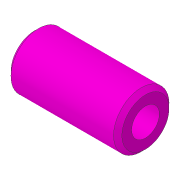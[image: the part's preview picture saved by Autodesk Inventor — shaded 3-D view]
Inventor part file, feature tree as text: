
AUTODESK INVENTOR PART (.ipt)
format: ipt  version: 2019.4 (Build 234330000, 330)  size: 90,112 bytes
history: native  units: mm
features: other x1, extrude x1, chamfer x1, sketch x1
ambient origin geometry x8: Origin, YZ Plane, XZ Plane, XY Plane, X Axis, Y Axis, Z Axis, Center Point
bodies: Body1 (feature_tree)
feature tree (4):
  other  "ソリッド1"
  extrude  "押し出し1"  Depth=4.0mm
  chamfer  "面取り1"  Distance=2.0mm
  sketch  "スケッチ1"
